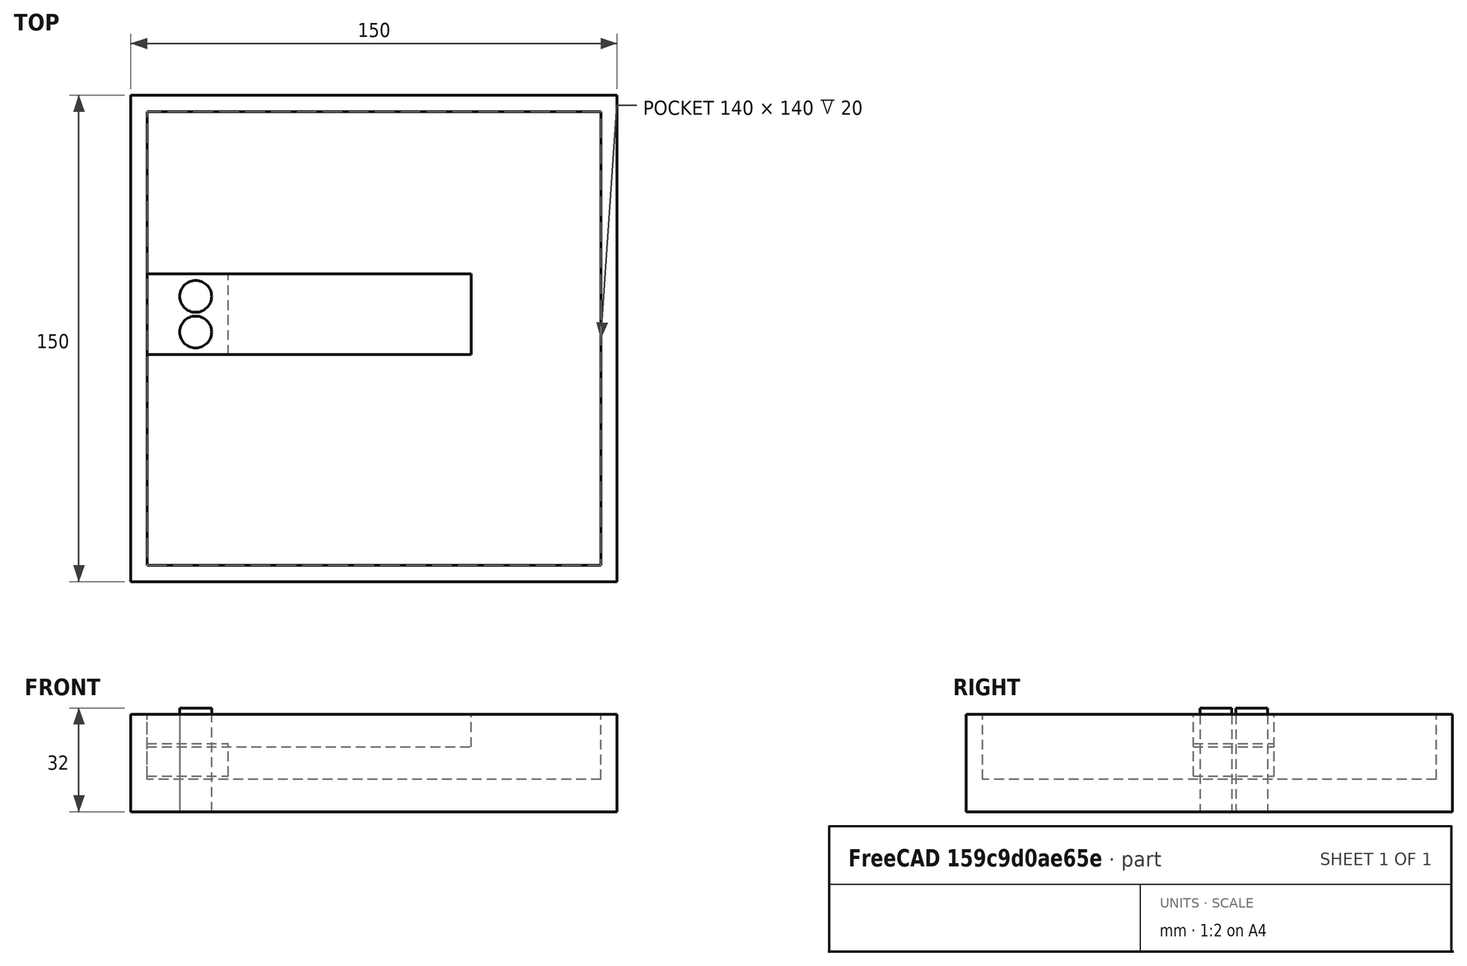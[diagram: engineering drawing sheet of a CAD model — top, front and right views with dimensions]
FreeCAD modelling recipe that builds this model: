
FCSTD DOCUMENT
Label: loadSetup
objects: Part::Extrusion×7, Part::Part2DObjectPython×6, App::DocumentObjectGroup×1, Part::Cut×1
note: 14 computed .brp shape members not serialized (recipe doc carries the construction recipe); baked Part::Feature solids carry a one-line shape summary decoded from their .brp

FEATURE [App::DocumentObjectGroup] Group
FEATURE [Part::Part2DObjectPython] Rectangle  # Draft 2D object (typed FeaturePython)
  FilletRadius = 0
  Height = 150
  Length = 150
FEATURE [Part::Extrusion] Extrude
  Base = -> Rectangle
  Dir = (0,0,30)
  Solid = false
FEATURE [Part::Part2DObjectPython] Rectangle001  # Draft 2D object (typed FeaturePython)
  FilletRadius = 0
  Height = 140
  Length = 140
  Placement = pos=(5,5,10) rot=(0,0,1;0rad)
FEATURE [Part::Extrusion] Extrude001
  Base = -> Rectangle001
  Dir = (0,0,50)
  Solid = false
FEATURE [Part::Cut] Cut
  Base = -> Extrude
  Tool = -> Extrude001
FEATURE [Part::Part2DObjectPython] Rectangle002  # Draft 2D object (typed FeaturePython)
  FilletRadius = 0
  Height = 25
  Length = 100
  Placement = pos=(5,70,20) rot=(0,0,1;0rad)
FEATURE [Part::Extrusion] Extrude002
  Base = -> Rectangle002
  Dir = (0,0,10)
  Solid = false
FEATURE [Part::Part2DObjectPython] Rectangle003  # Draft 2D object (typed FeaturePython)
  FilletRadius = 0
  Height = 25
  Length = 25
  Placement = pos=(5,70,11) rot=(0,0,1;0rad)
FEATURE [Part::Extrusion] Extrude003
  Base = -> Rectangle003
  Dir = (0,0,10)
  Solid = false
FEATURE [Part::Part2DObjectPython] Circle  label="screw1"  # Draft 2D object (typed FeaturePython)
  FirstAngle = 0
  LastAngle = 0
  Placement = pos=(20,77,0) rot=(0,0,1;0rad)
  Radius = 4.91853
FEATURE [Part::Part2DObjectPython] Circle001  label="screw2"  # Draft 2D object (typed FeaturePython)
  FirstAngle = 0
  LastAngle = 0
  Placement = pos=(20,88,0) rot=(0,0,1;0rad)
  Radius = 4.91853
FEATURE [Part::Extrusion] Extrude004
  Base = -> Circle
  Dir = (0,0,30)
  Solid = false
FEATURE [Part::Extrusion] Extrude005
  Base = -> Circle
  Dir = (0,0,32)
  Solid = false
FEATURE [Part::Extrusion] Extrude006
  Base = -> Circle001
  Dir = (0,0,32)
  Solid = false
